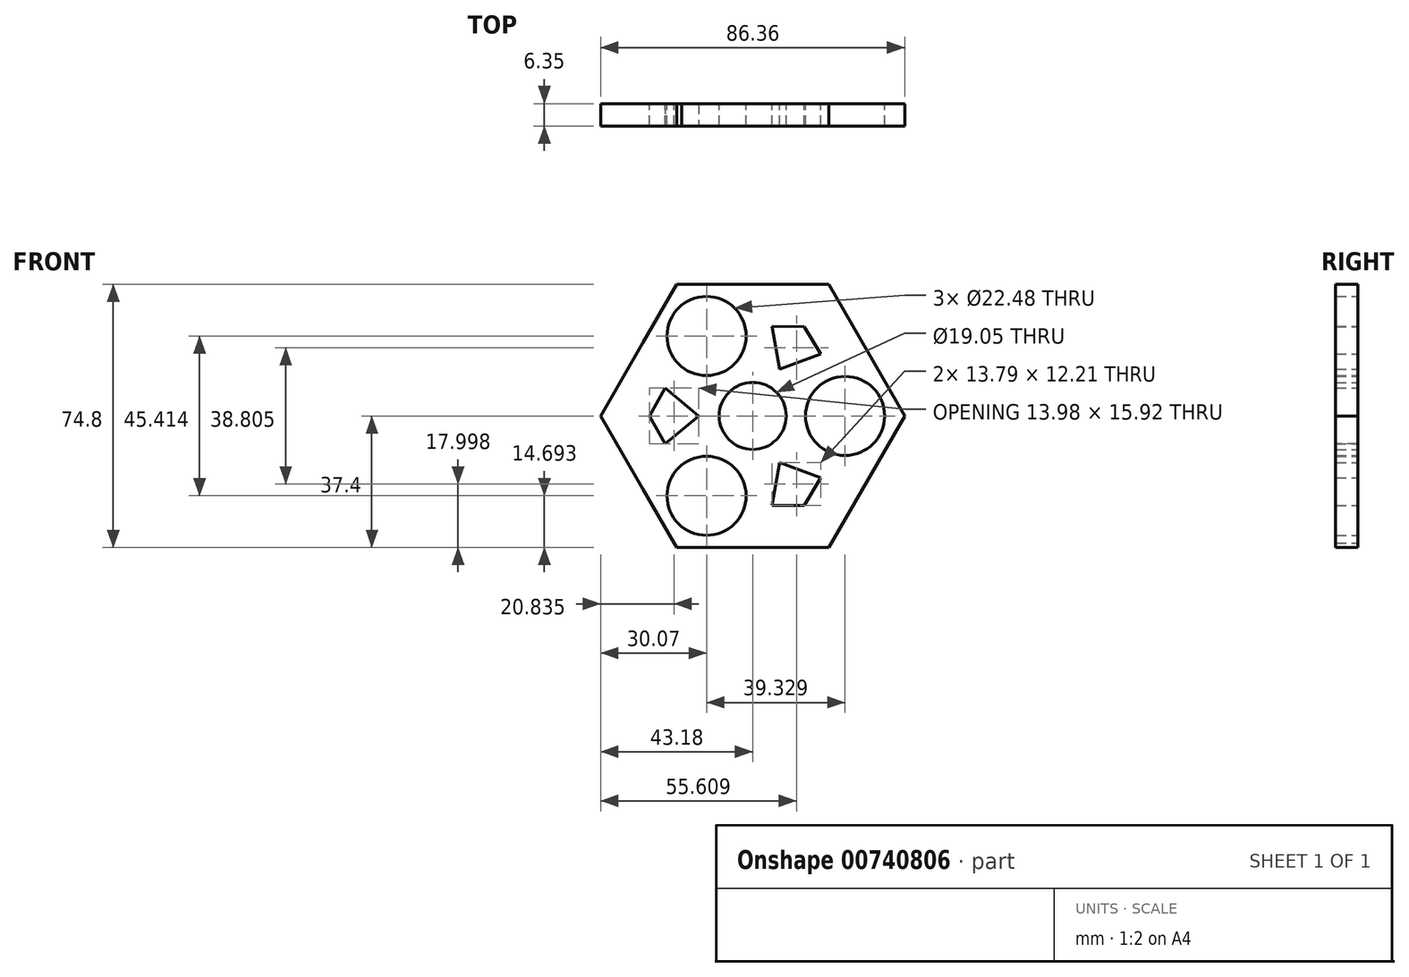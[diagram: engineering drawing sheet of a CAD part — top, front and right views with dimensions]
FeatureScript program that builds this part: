
annotation { "Feature Type Name" : "Feature", "Feature Type Description" : "" }
export const myFeature = defineFeature(function(context is Context, id is Id, definition is map)
    precondition{}
    {
        {
            var Q0;
            Q0=qCreatedBy(makeId("Front.planeOp"),FACE);
            var sketch = newSketch(context, id + "F0", { "sketchPlane" : qUnion([Q0])});
            skLineSegment(sketch, "E0.0", {"start": v(33.57, 16.65) * mm, "end": v(42.45, 1.27) * mm});
            skLineSegment(sketch, "E0.1", {"start": v(42.45, -1.27) * mm, "end": v(33.57, -16.65) * mm});
            skLineSegment(sketch, "E0.2", {"start": v(-2.36, -37.4) * mm, "end": v(-20.12, -37.4) * mm});
            skLineSegment(sketch, "E0.3", {"start": v(-22.32, -36.13) * mm, "end": v(-31.2, -20.75) * mm});
            skLineSegment(sketch, "E0.4", {"start": v(-31.2, 20.75) * mm, "end": v(-22.32, 36.13) * mm});
            skLineSegment(sketch, "E0.5", {"start": v(-20.12, 37.4) * mm, "end": v(-2.36, 37.4) * mm});
            skPoint(sketch, "E0.0.midPoint", {"position": v(32.38, 18.7) * mm});
            skPoint(sketch, "E1.visualSharp", {"position": v(-43.18, 0) * mm});
            skPoint(sketch, "E2.visualSharp", {"position": v(-21.6, 37.4) * mm});
            skArc(sketch, "E2.filletArc", {"start": v(-20.12, 37.4) * mm, "mid": v(-21.4, 37.05) * mm, "end": v(-22.32, 36.13) * mm});
            skPoint(sketch, "E3.visualSharp", {"position": v(21.6, 37.4) * mm});
            skPoint(sketch, "E4.visualSharp", {"position": v(43.18, 0) * mm});
            skArc(sketch, "E4.filletArc", {"start": v(42.45, -1.27) * mm, "mid": v(42.79, 0) * mm, "end": v(42.45, 1.27) * mm});
            skPoint(sketch, "E5.visualSharp", {"position": v(21.6, -37.4) * mm});
            skPoint(sketch, "E6.visualSharp", {"position": v(-21.6, -37.4) * mm});
            skArc(sketch, "E6.filletArc", {"start": v(-22.32, -36.13) * mm, "mid": v(-21.4, -37.05) * mm, "end": v(-20.12, -37.4) * mm});
            skCircle(sketch, "E7", {"center": v(0, 0) * mm, "radius": 9.53 * mm});
            skCircle(sketch, "E8", {"center": v(-13.1, -22.7) * mm, "radius": 11.24 * mm});
            skCircle(sketch, "E9.MirrorC", {"center": v(26.22, 0) * mm, "radius": 11.24 * mm});
            skCircle(sketch, "E10.MirrorC", {"center": v(-13.1, 22.7) * mm, "radius": 11.24 * mm});
            skLineSegment(sketch, "E11.trimOffspring", {"start": v(-21.4, -37.05) * mm, "end": v(-21.6, -37.4) * mm});
            skLineSegment(sketch, "E12", {"start": v(-2.36, -37.4) * mm, "end": v(-2.32, -37.32) * mm});
            skLineSegment(sketch, "E13", {"start": v(7.66, -13.39) * mm, "end": v(7.68, -13.3) * mm});
            skLineSegment(sketch, "E14.MirrorCS", {"start": v(7.66, 13.39) * mm, "end": v(7.68, 13.3) * mm});
            skLineSegment(sketch, "E15.MirrorCS", {"start": v(33.57, -16.65) * mm, "end": v(42.45, -1.27) * mm});
            skPoint(sketch, "E16.MirrorCS.end.orphan", {"position": v(42.45, -73.52) * mm});
            skPoint(sketch, "E16.MirrorCS.start.orphan", {"position": v(22.32, -38.67) * mm});
            skPoint(sketch, "E17.MirrorCS.end.orphan", {"position": v(20.12, -37.4) * mm});
            skPoint(sketch, "E17.MirrorCS.start.orphan", {"position": v(0, -37.4) * mm});
            skPoint(sketch, "E18.orphan", {"position": v(22.32, -36.13) * mm});
            skLineSegment(sketch, "E19.MirrorCS", {"start": v(-24.82, -7.89) * mm, "end": v(-15.35, 0) * mm});
            skLineSegment(sketch, "E20.MirrorCS", {"start": v(-24.82, 7.89) * mm, "end": v(-15.35, 0) * mm});
            skLineSegment(sketch, "E21.MirrorCS", {"start": v(-31.2, 20.75) * mm, "end": v(-31.16, 20.67) * mm});
            skLineSegment(sketch, "E22.MirrorCS", {"start": v(-31.2, -20.75) * mm, "end": v(-31.16, -20.67) * mm});
            skPoint(sketch, "E1.filletArc.end.orphan", {"position": v(-42.45, -1.27) * mm});
            skLineSegment(sketch, "E23", {"start": v(-15.35, 0) * mm, "end": v(-24.82, 7.89) * mm});
            skCircle(sketch, "E24.cCircle", {"center": v(0, 0) * mm, "radius": 37.4 * mm, "construction": true});
            skLineSegment(sketch, "E24.0", {"start": v(33.57, 16.65) * mm, "end": v(43.18, 0) * mm});
            skLineSegment(sketch, "E24.1", {"start": v(43.18, 0) * mm, "end": v(21.6, -37.4) * mm});
            skLineSegment(sketch, "E24.2", {"start": v(21.6, -37.4) * mm, "end": v(-21.59, -37.4) * mm});
            skLineSegment(sketch, "E24.3", {"start": v(-21.59, -37.4) * mm, "end": v(-43.18, 0) * mm});
            skLineSegment(sketch, "E24.4", {"start": v(-43.18, 0) * mm, "end": v(-21.6, 37.4) * mm});
            skLineSegment(sketch, "E24.5", {"start": v(-21.6, 37.4) * mm, "end": v(-2.36, 37.4) * mm});
            skPoint(sketch, "E25.MirrorCS.start.orphan", {"position": v(16.1, -34.22) * mm});
            skPoint(sketch, "E26.0.start.orphan", {"position": v(21.6, -31.04) * mm});
            skPoint(sketch, "E27.orphan", {"position": v(21.59, 37.4) * mm});
            skLineSegment(sketch, "E28.0", {"start": v(-29.34, 0) * mm, "end": v(-24.86, 7.96) * mm});
            skLineSegment(sketch, "E29.MirrorCS", {"start": v(-29.34, 0) * mm, "end": v(-24.86, -7.96) * mm});
            skPoint(sketch, "E30.orphan", {"position": v(-30.93, -2.84) * mm});
            skPoint(sketch, "E31.orphan", {"position": v(-30.93, 2.84) * mm});
            skPoint(sketch, "E32.orphan", {"position": v(-23.05, 11.17) * mm});
            skPoint(sketch, "E33.orphan", {"position": v(-23.05, -11.17) * mm});
            skLineSegment(sketch, "E34.trimOffspring", {"start": v(-24.86, -7.96) * mm, "end": v(-24.82, -7.89) * mm});
            skLineSegment(sketch, "E35.trimOffspring", {"start": v(-24.86, 7.96) * mm, "end": v(-24.82, 7.89) * mm});
            skLineSegment(sketch, "E36", {"start": v(0, 0) * mm, "end": v(-4.76, 8.25) * mm});
            skLineSegment(sketch, "E37.MirrorCS", {"start": v(14.67, 25.4) * mm, "end": v(5.53, 25.5) * mm});
            skLineSegment(sketch, "E38.MirrorCS", {"start": v(14.67, 25.4) * mm, "end": v(19.32, 17.55) * mm});
            skLineSegment(sketch, "E39.MirrorCS", {"start": v(14.67, -25.4) * mm, "end": v(19.32, -17.55) * mm});
            skLineSegment(sketch, "E40.MirrorCS", {"start": v(14.67, -25.4) * mm, "end": v(5.53, -25.5) * mm});
            skLineSegment(sketch, "E41.MirrorCS", {"start": v(43.18, 0) * mm, "end": v(21.6, 37.4) * mm});
            skLineSegment(sketch, "E42.MirrorCS", {"start": v(21.6, 37.4) * mm, "end": v(-21.59, 37.4) * mm});
            skLineSegment(sketch, "E43", {"start": v(7.68, -13.3) * mm, "end": v(19.32, -17.55) * mm});
            skPoint(sketch, "E44.MirrorCS.start.orphan", {"position": v(19.24, -17.55) * mm});
            skLineSegment(sketch, "E45", {"start": v(5.53, -25.5) * mm, "end": v(7.68, -13.3) * mm});
            skPoint(sketch, "E46.trimOffspring.end.orphan", {"position": v(5.58, -25.44) * mm});
            skLineSegment(sketch, "E47", {"start": v(5.53, 25.5) * mm, "end": v(7.68, 13.3) * mm});
            skPoint(sketch, "E48.trimOffspring.end.orphan", {"position": v(5.58, 25.44) * mm});
            skLineSegment(sketch, "E49", {"start": v(19.32, 17.55) * mm, "end": v(7.68, 13.3) * mm});
            skPoint(sketch, "E50.MirrorCS.start.orphan", {"position": v(19.24, 17.55) * mm});
            skSolve(sketch);
        }
        {
            var Q0;
            Q0=qSketchRegion(id+"F0",true);
            extrude(context, id + "F1", {"entities" : qUnion([Q0]), "depth" : 6.35 * mm, "offsetDistance" : 25.4 * mm});
        }
    });
